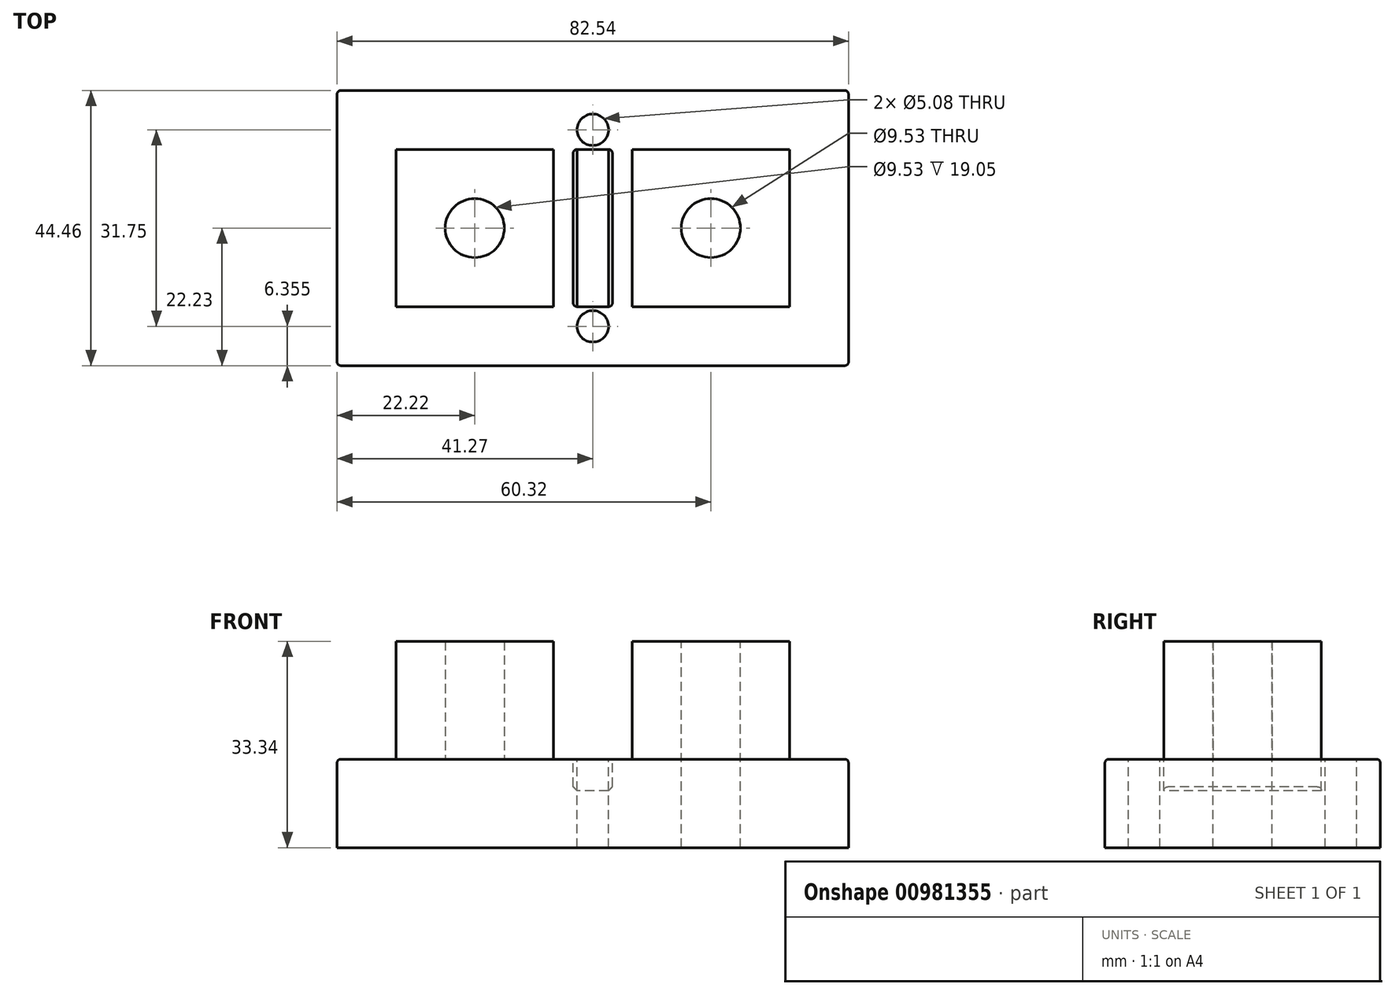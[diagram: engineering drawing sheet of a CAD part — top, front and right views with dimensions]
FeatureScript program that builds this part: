
annotation { "Feature Type Name" : "Feature", "Feature Type Description" : "" }
export const myFeature = defineFeature(function(context is Context, id is Id, definition is map)
    precondition{}
    {
        {
            var Q0;
            Q0=qCreatedBy(makeId("Top.planeOp"),FACE);
            var sketch = newSketch(context, id + "F0", { "sketchPlane" : qUnion([Q0])});
            skLineSegment(sketch, "E0.bottom", {"start": v(41.28, 22.23) * mm, "end": v(-41.28, 22.23) * mm});
            skLineSegment(sketch, "E0.top", {"start": v(41.28, -22.23) * mm, "end": v(-41.28, -22.23) * mm});
            skLineSegment(sketch, "E0.left", {"start": v(41.28, 22.23) * mm, "end": v(41.28, -22.23) * mm});
            skLineSegment(sketch, "E0.right", {"start": v(-41.28, 22.23) * mm, "end": v(-41.28, -22.23) * mm});
            skPoint(sketch, "E0.middle", {"position": v(0, 0) * mm});
            skLineSegment(sketch, "E1.bottom", {"start": v(31.75, 12.7) * mm, "end": v(6.35, 12.7) * mm});
            skLineSegment(sketch, "E1.top", {"start": v(31.75, -12.7) * mm, "end": v(6.35, -12.7) * mm});
            skLineSegment(sketch, "E1.left", {"start": v(31.75, 12.7) * mm, "end": v(31.75, -12.7) * mm});
            skLineSegment(sketch, "E1.right", {"start": v(-31.75, 12.7) * mm, "end": v(-31.75, -12.7) * mm});
            skLineSegment(sketch, "E2.bottom", {"start": v(6.35, 12.7) * mm, "end": v(-6.35, 12.7) * mm});
            skLineSegment(sketch, "E2.top", {"start": v(6.35, -12.7) * mm, "end": v(-6.35, -12.7) * mm});
            skLineSegment(sketch, "E2.left", {"start": v(6.35, 12.7) * mm, "end": v(6.35, -12.7) * mm});
            skLineSegment(sketch, "E2.right", {"start": v(-6.35, 12.7) * mm, "end": v(-6.35, 12.7) * mm});
            skLineSegment(sketch, "E3", {"start": v(-6.35, 12.7) * mm, "end": v(-6.35, -12.7) * mm});
            skLineSegment(sketch, "E4", {"start": v(-6.35, -12.7) * mm, "end": v(-31.75, -12.7) * mm});
            skLineSegment(sketch, "E5", {"start": v(-6.35, 12.7) * mm, "end": v(-31.75, 12.7) * mm});
            skCircle(sketch, "E6", {"center": v(-19.05, 0) * mm, "radius": 4.76 * mm});
            skCircle(sketch, "E7.MirrorC", {"center": v(19.05, 0) * mm, "radius": 4.76 * mm});
            skLineSegment(sketch, "E8.bottom", {"start": v(3.18, 22.23) * mm, "end": v(-3.18, 22.23) * mm});
            skLineSegment(sketch, "E8.top", {"start": v(3.18, -22.23) * mm, "end": v(-3.18, -22.23) * mm});
            skLineSegment(sketch, "E8.left", {"start": v(3.18, 22.23) * mm, "end": v(3.18, -22.23) * mm});
            skLineSegment(sketch, "E8.right", {"start": v(-3.18, 22.23) * mm, "end": v(-3.18, -22.23) * mm});
            skCircle(sketch, "E9", {"center": v(0, -15.88) * mm, "radius": 2.54 * mm});
            skLineSegment(sketch, "E10.bottom", {"start": v(-2.54, -22.23) * mm, "end": v(2.54, -22.23) * mm});
            skLineSegment(sketch, "E10.top", {"start": v(-2.54, 22.23) * mm, "end": v(2.54, 22.23) * mm});
            skCircle(sketch, "E11", {"center": v(0, 15.88) * mm, "radius": 2.54 * mm});
            skSolve(sketch);
        }
        {
            var Q0;
            {var subQ0=sQuery(id+"F0.wireOp",EDGE,"E0.right");Q0=makeQuery(id+"F0.imprint","IMPRINT",FACE,{"disambiguationData":[TD([[makeQuery(id+"F0.imprint","IMPRINT",EDGE,{"derivedFrom":subQ0}),1.0]])]});}
            var Q1;
            Q1=makeQuery(id+"F0.imprint","IMPRINT",FACE,{"disambiguationData":[TD([[makeQuery(id+"F0.imprint","IMPRINT",EDGE,{"derivedFrom":sQuery(id+"F0.wireOp",EDGE,"E1.right")}),1.0]])]});
            var Q2;
            {var subQ0=sQuery(id+"F0.wireOp",EDGE,"E3");Q2=makeQuery(id+"F0.imprint","IMPRINT",FACE,{"disambiguationData":[TD([[makeQuery(id+"F0.imprint","IMPRINT",EDGE,{"derivedFrom":subQ0}),1.0]])]});}
            var Q3;
            {var subQ0=sQuery(id+"F0.wireOp",EDGE,"E8.left");var subQ1=sQuery(id+"F0.wireOp",EDGE,"E2.top");var subQ2=makeQuery(id+"F0.imprint","INTERSECT",VERTEX,{"derivedFrom":[subQ1,subQ0]});Q3=makeQuery(id+"F0.imprint","IMPRINT",FACE,{"disambiguationData":[TD([[makeQuery(id+"F0.imprint","IMPRINT",EDGE,{"disambiguationData":[TD([[subQ2,-1.0]])],"derivedFrom":subQ1}),-1.0]])]});}
            var Q4;
            {var subQ5=sQuery(id+"F0.wireOp",EDGE,"E8.bottom");Q4=makeQuery(id+"F0.imprint","IMPRINT",FACE,{"disambiguationData":[TD([[makeQuery(id+"F0.imprint","IMPRINT",EDGE,{"derivedFrom":subQ5}),1.0]])]});}
            var Q5;
            {var subQ5=sQuery(id+"F0.wireOp",EDGE,"E8.top");Q5=makeQuery(id+"F0.imprint","IMPRINT",FACE,{"disambiguationData":[TD([[makeQuery(id+"F0.imprint","IMPRINT",EDGE,{"derivedFrom":subQ5}),-1.0]])]});}
            var Q6;
            {var subQ1=sQuery(id+"F0.wireOp",EDGE,"E0.left");Q6=makeQuery(id+"F0.imprint","IMPRINT",FACE,{"disambiguationData":[TD([[makeQuery(id+"F0.imprint","IMPRINT",EDGE,{"derivedFrom":subQ1}),-1.0]])]});}
            var Q7;
            {var subQ0=sQuery(id+"F0.wireOp",EDGE,"E2.left");Q7=makeQuery(id+"F0.imprint","IMPRINT",FACE,{"disambiguationData":[TD([[makeQuery(id+"F0.imprint","IMPRINT",EDGE,{"derivedFrom":subQ0}),-1.0]])]});}
            var Q8;
            Q8=makeQuery(id+"F0.imprint","IMPRINT",FACE,{"disambiguationData":[TD([[makeQuery(id+"F0.imprint","IMPRINT",EDGE,{"derivedFrom":sQuery(id+"F0.wireOp",EDGE,"E1.bottom")}),1.0]])]});
            var Q9;
            Q9=makeQuery(id+"F0.imprint","IMPRINT",FACE,{"disambiguationData":[TD([[makeQuery(id+"F0.imprint","IMPRINT",EDGE,{"derivedFrom":sQuery(id+"F0.wireOp",EDGE,"E7.MirrorC")}),-1.0]])]});
            var Q10;
            Q10=makeQuery(id+"F0.imprint","IMPRINT",FACE,{"disambiguationData":[TD([[makeQuery(id+"F0.imprint","IMPRINT",EDGE,{"derivedFrom":sQuery(id+"F0.wireOp",EDGE,"E6")}),1.0]])]});
            var Q11;
            {var subQ5=sQuery(id+"F0.wireOp",EDGE,"E10.bottom");Q11=makeQuery(id+"F0.imprint","IMPRINT",FACE,{"disambiguationData":[TD([[makeQuery(id+"F0.imprint","IMPRINT",EDGE,{"derivedFrom":subQ5}),1.0]])]});}
            var Q12;
            {var subQ0=sQuery(id+"F0.wireOp",EDGE,"E10.right");var subQ1=sQuery(id+"F0.wireOp",EDGE,"E2.top");var subQ2=makeQuery(id+"F0.imprint","INTERSECT",VERTEX,{"derivedFrom":[subQ1,subQ0]});Q12=makeQuery(id+"F0.imprint","IMPRINT",FACE,{"disambiguationData":[TD([[makeQuery(id+"F0.imprint","IMPRINT",EDGE,{"disambiguationData":[TD([[subQ2,-1.0]])],"derivedFrom":subQ1}),1.0]])]});}
            var Q13;
            {var subQ0=sQuery(id+"F0.wireOp",EDGE,"E10.right");var subQ1=sQuery(id+"F0.wireOp",EDGE,"E2.top");var subQ2=makeQuery(id+"F0.imprint","INTERSECT",VERTEX,{"derivedFrom":[subQ1,subQ0]});Q13=makeQuery(id+"F0.imprint","IMPRINT",FACE,{"disambiguationData":[TD([[makeQuery(id+"F0.imprint","IMPRINT",EDGE,{"disambiguationData":[TD([[subQ2,-1.0]])],"derivedFrom":subQ1}),-1.0]])]});}
            var Q14;
            {var subQ0=sQuery(id+"F0.wireOp",EDGE,"E9");var subQ1=makeQuery(id+"F0.imprint","INTERSECT",VERTEX,{"derivedFrom":[subQ0,sQuery(id+"F0.wireOp",EDGE,"E10.left")]});Q14=makeQuery(id+"F0.imprint","IMPRINT",FACE,{"disambiguationData":[TD([[makeQuery(id+"F0.imprint","IMPRINT",EDGE,{"disambiguationData":[TD([[subQ1,1.0]])],"derivedFrom":subQ0}),1.0]])]});}
            var Q15;
            {var subQ0=sQuery(id+"F0.wireOp",EDGE,"E11");var subQ1=makeQuery(id+"F0.imprint","INTERSECT",VERTEX,{"derivedFrom":[sQuery(id+"F0.wireOp",EDGE,"E10.left"),subQ0]});Q15=makeQuery(id+"F0.imprint","IMPRINT",FACE,{"disambiguationData":[TD([[makeQuery(id+"F0.imprint","IMPRINT",EDGE,{"disambiguationData":[TD([[subQ1,1.0]])],"derivedFrom":subQ0}),1.0]])]});}
            var Q16;
            {var subQ0=sQuery(id+"F0.wireOp",EDGE,"E10.top");Q16=makeQuery(id+"F0.imprint","IMPRINT",FACE,{"disambiguationData":[TD([[makeQuery(id+"F0.imprint","IMPRINT",EDGE,{"derivedFrom":subQ0}),-1.0]])]});}
            var Q17;
            {var subQ0=sQuery(id+"F0.wireOp",EDGE,"E10.left");var subQ1=sQuery(id+"F0.wireOp",EDGE,"E2.top");var subQ2=makeQuery(id+"F0.imprint","INTERSECT",VERTEX,{"derivedFrom":[subQ1,subQ0]});Q17=makeQuery(id+"F0.imprint","IMPRINT",FACE,{"disambiguationData":[TD([[makeQuery(id+"F0.imprint","IMPRINT",EDGE,{"disambiguationData":[TD([[subQ2,-1.0]])],"derivedFrom":subQ1}),-1.0]])]});}
            var Q18;
            {var subQ0=sQuery(id+"F0.wireOp",EDGE,"E10.right");var subQ1=sQuery(id+"F0.wireOp",EDGE,"E2.bottom");var subQ2=makeQuery(id+"F0.imprint","INTERSECT",VERTEX,{"derivedFrom":[subQ1,subQ0]});Q18=makeQuery(id+"F0.imprint","IMPRINT",FACE,{"disambiguationData":[TD([[makeQuery(id+"F0.imprint","IMPRINT",EDGE,{"disambiguationData":[TD([[subQ2,-1.0]])],"derivedFrom":subQ1}),-1.0]])]});}
            extrude(context, id + "F1", {"entities" : qUnion([Q0, Q1, Q2, Q3, Q4, Q5, Q6, Q7, Q8, Q9, Q10, Q11, Q12, Q13, Q14, Q15, Q16, Q17, Q18]), "oppositeDirection" : true, "depth" : 14.29 * mm, "offsetDistance" : 25.4 * mm});
        }
        {
            var Q0;
            Q0=makeQuery(id+"F0.imprint","IMPRINT",FACE,{"disambiguationData":[TD([[makeQuery(id+"F0.imprint","IMPRINT",EDGE,{"derivedFrom":sQuery(id+"F0.wireOp",EDGE,"E1.right")}),1.0]])]});
            var Q1;
            Q1=makeQuery(id+"F0.imprint","IMPRINT",FACE,{"disambiguationData":[TD([[makeQuery(id+"F0.imprint","IMPRINT",EDGE,{"derivedFrom":sQuery(id+"F0.wireOp",EDGE,"E1.bottom")}),1.0]])]});
            extrude(context, id + "F2", {"entities" : qUnion([Q0, Q1]), "operationType" : NewBodyOperationType.ADD, "depth" : 19.05 * mm, "offsetDistance" : 25.4 * mm});
        }
        {
            var Q0;
            {var subQ0=sQuery(id+"F0.wireOp",EDGE,"E8.left");var subQ1=sQuery(id+"F0.wireOp",EDGE,"E2.top");var subQ2=makeQuery(id+"F0.imprint","INTERSECT",VERTEX,{"derivedFrom":[subQ1,subQ0]});Q0=makeQuery(id+"F0.imprint","IMPRINT",FACE,{"disambiguationData":[TD([[makeQuery(id+"F0.imprint","IMPRINT",EDGE,{"disambiguationData":[TD([[subQ2,-1.0]])],"derivedFrom":subQ1}),-1.0]])]});}
            var Q1;
            {var subQ5=sQuery(id+"F0.wireOp",EDGE,"E8.top");Q1=makeQuery(id+"F0.imprint","IMPRINT",FACE,{"disambiguationData":[TD([[makeQuery(id+"F0.imprint","IMPRINT",EDGE,{"derivedFrom":subQ5}),-1.0]])]});}
            var Q2;
            {var subQ5=sQuery(id+"F0.wireOp",EDGE,"E8.bottom");Q2=makeQuery(id+"F0.imprint","IMPRINT",FACE,{"disambiguationData":[TD([[makeQuery(id+"F0.imprint","IMPRINT",EDGE,{"derivedFrom":subQ5}),1.0]])]});}
            extrude(context, id + "F3", {"entities" : qUnion([Q0, Q1, Q2]), "operationType" : NewBodyOperationType.REMOVE, "oppositeDirection" : true, "depth" : 5.08 * mm, "offsetDistance" : 25.4 * mm});
        }
        {
            var Q0;
            Q0=makeQuery(id+"F0.imprint","IMPRINT",FACE,{"disambiguationData":[TD([[makeQuery(id+"F0.imprint","IMPRINT",EDGE,{"derivedFrom":sQuery(id+"F0.wireOp",EDGE,"E9")}),1.0]])]});
            var Q1;
            Q1=makeQuery(id+"F0.imprint","IMPRINT",FACE,{"disambiguationData":[TD([[makeQuery(id+"F0.imprint","IMPRINT",EDGE,{"derivedFrom":sQuery(id+"F0.wireOp",EDGE,"E11")}),1.0]])]});
            extrude(context, id + "F4", {"entities" : qUnion([Q0, Q1]), "operationType" : NewBodyOperationType.REMOVE, "oppositeDirection" : true, "depth" : 14.29 * mm, "offsetDistance" : 25.4 * mm});
        }
        {
            var Q0;
            Q0=makeQuery(id+"F3.boolean.opBoolean","COPY",EDGE,{"derivedFrom":makeQuery(id+"F3.opExtrude","CAP_EDGE",EDGE,{"disambiguationData":[OSD([sQuery(id+"F0.wireOp",EDGE,"E8.left")])],"isStart":false})});
            var Q1;
            Q1=makeQuery(id+"F3.boolean.opBoolean","COPY",EDGE,{"derivedFrom":makeQuery(id+"F3.opExtrude","CAP_EDGE",EDGE,{"disambiguationData":[OSD([sQuery(id+"F0.wireOp",EDGE,"E8.right")])],"isStart":false})});
            var Q2;
            Q2=makeQuery(id+"F3.boolean.opBoolean","COPY",EDGE,{"derivedFrom":makeQuery(id+"F3.opExtrude","CAP_EDGE",EDGE,{"disambiguationData":[OSD([sQuery(id+"F0.wireOp",EDGE,"E8.left")])],"isStart":true})});
            var Q3;
            Q3=makeQuery(id+"F3.boolean.opBoolean","COPY",EDGE,{"derivedFrom":makeQuery(id+"F3.opExtrude","CAP_EDGE",EDGE,{"disambiguationData":[OSD([sQuery(id+"F0.wireOp",EDGE,"E8.right")])],"isStart":true})});
            chamfer(context, id + "F5", {"entities" : qUnion([Q0, Q1, Q2, Q3]), "width" : 0.64 * mm, "tangentPropagation" : true});
        }
        {
            var Q0;
            {var subQ0=sQuery(id+"F0.wireOp",EDGE,"E10.bottom");var subQ1=sQuery(id+"F0.wireOp",EDGE,"E8.top");var subQ2=sQuery(id+"F0.wireOp",EDGE,"E0.right");var subQ3=sQuery(id+"F0.wireOp",EDGE,"E0.top");Q0=makeQuery(id+"F3.boolean.opBoolean","SPLIT",EDGE,{"disambiguationData":[TD([makeQuery(id+"F1.opExtrude","SWEPT_FACE",FACE,{"disambiguationData":[OSD([subQ2])]})])],"derivedFrom":makeQuery(id+"F1.opExtrude","CAP_EDGE",EDGE,{"disambiguationData":[OSD([subQ3,subQ1,subQ0])],"isStart":true})});}
            var Q1;
            Q1=makeQuery(id+"F5.opChamfer","BLEND_EDGE",EDGE,{"blendedFrom":[makeQuery(id+"F3.boolean.opBoolean","COPY",EDGE,{"derivedFrom":makeQuery(id+"F3.opExtrude","CAP_EDGE",EDGE,{"disambiguationData":[OSD([sQuery(id+"F0.wireOp",EDGE,"E8.right")])],"isStart":true})}),makeQuery(id+"F1.opExtrude","SWEPT_FACE",FACE,{"disambiguationData":[OSD([sQuery(id+"F0.wireOp",EDGE,"E0.top"),sQuery(id+"F0.wireOp",EDGE,"E8.top"),sQuery(id+"F0.wireOp",EDGE,"E10.bottom")])]})],"blendedInto":[makeQuery(id+"F1.opExtrude","SWEPT_FACE",FACE,{"disambiguationData":[OSD([sQuery(id+"F0.wireOp",EDGE,"E0.top"),sQuery(id+"F0.wireOp",EDGE,"E8.top"),sQuery(id+"F0.wireOp",EDGE,"E10.bottom")])]})]});
            var Q2;
            Q2=makeQuery(id+"F5.opChamfer","BLEND_EDGE",EDGE,{"blendedFrom":[makeQuery(id+"F3.boolean.opBoolean","COPY",EDGE,{"derivedFrom":makeQuery(id+"F3.opExtrude","CAP_EDGE",EDGE,{"disambiguationData":[OSD([sQuery(id+"F0.wireOp",EDGE,"E8.right")])],"isStart":false})}),makeQuery(id+"F1.opExtrude","SWEPT_FACE",FACE,{"disambiguationData":[OSD([sQuery(id+"F0.wireOp",EDGE,"E0.top"),sQuery(id+"F0.wireOp",EDGE,"E8.top"),sQuery(id+"F0.wireOp",EDGE,"E10.bottom")])]})],"blendedInto":[makeQuery(id+"F1.opExtrude","SWEPT_FACE",FACE,{"disambiguationData":[OSD([sQuery(id+"F0.wireOp",EDGE,"E0.top"),sQuery(id+"F0.wireOp",EDGE,"E8.top"),sQuery(id+"F0.wireOp",EDGE,"E10.bottom")])]})]});
            var Q3;
            Q3=makeQuery(id+"F3.boolean.opBoolean","COPY",EDGE,{"derivedFrom":makeQuery(id+"F3.opExtrude","CAP_EDGE",EDGE,{"disambiguationData":[OSD([sQuery(id+"F0.wireOp",EDGE,"E8.top"),sQuery(id+"F0.wireOp",EDGE,"E10.bottom")])],"isStart":false})});
            var Q4;
            Q4=makeQuery(id+"F5.opChamfer","BLEND_EDGE",EDGE,{"blendedFrom":[makeQuery(id+"F3.boolean.opBoolean","COPY",EDGE,{"derivedFrom":makeQuery(id+"F3.opExtrude","CAP_EDGE",EDGE,{"disambiguationData":[OSD([sQuery(id+"F0.wireOp",EDGE,"E8.left")])],"isStart":false})}),makeQuery(id+"F1.opExtrude","SWEPT_FACE",FACE,{"disambiguationData":[OSD([sQuery(id+"F0.wireOp",EDGE,"E0.top"),sQuery(id+"F0.wireOp",EDGE,"E8.top"),sQuery(id+"F0.wireOp",EDGE,"E10.bottom")])]})],"blendedInto":[makeQuery(id+"F1.opExtrude","SWEPT_FACE",FACE,{"disambiguationData":[OSD([sQuery(id+"F0.wireOp",EDGE,"E0.top"),sQuery(id+"F0.wireOp",EDGE,"E8.top"),sQuery(id+"F0.wireOp",EDGE,"E10.bottom")])]})]});
            var Q5;
            Q5=makeQuery(id+"F3.boolean.opBoolean","COPY",EDGE,{"derivedFrom":makeQuery(id+"F3.opExtrude","SWEPT_EDGE",EDGE,{"disambiguationData":[OSD([sQuery(id+"F0.wireOp",EDGE,"E0.top"),sQuery(id+"F0.wireOp",EDGE,"E8.top"),sQuery(id+"F0.wireOp",EDGE,"E8.left")])]})});
            var Q6;
            Q6=makeQuery(id+"F5.opChamfer","BLEND_EDGE",EDGE,{"blendedFrom":[makeQuery(id+"F3.boolean.opBoolean","COPY",EDGE,{"derivedFrom":makeQuery(id+"F3.opExtrude","CAP_EDGE",EDGE,{"disambiguationData":[OSD([sQuery(id+"F0.wireOp",EDGE,"E8.left")])],"isStart":true})}),makeQuery(id+"F1.opExtrude","SWEPT_FACE",FACE,{"disambiguationData":[OSD([sQuery(id+"F0.wireOp",EDGE,"E0.top"),sQuery(id+"F0.wireOp",EDGE,"E8.top"),sQuery(id+"F0.wireOp",EDGE,"E10.bottom")])]})],"blendedInto":[makeQuery(id+"F1.opExtrude","SWEPT_FACE",FACE,{"disambiguationData":[OSD([sQuery(id+"F0.wireOp",EDGE,"E0.top"),sQuery(id+"F0.wireOp",EDGE,"E8.top"),sQuery(id+"F0.wireOp",EDGE,"E10.bottom")])]})]});
            var Q7;
            {var subQ0=sQuery(id+"F0.wireOp",EDGE,"E10.bottom");var subQ1=sQuery(id+"F0.wireOp",EDGE,"E8.top");var subQ2=sQuery(id+"F0.wireOp",EDGE,"E0.left");var subQ3=sQuery(id+"F0.wireOp",EDGE,"E0.top");Q7=makeQuery(id+"F3.boolean.opBoolean","SPLIT",EDGE,{"disambiguationData":[TD([makeQuery(id+"F1.opExtrude","SWEPT_FACE",FACE,{"disambiguationData":[OSD([subQ2])]})])],"derivedFrom":makeQuery(id+"F1.opExtrude","CAP_EDGE",EDGE,{"disambiguationData":[OSD([subQ3,subQ1,subQ0])],"isStart":true})});}
            var Q8;
            Q8=makeQuery(id+"F1.opExtrude","SWEPT_EDGE",EDGE,{"disambiguationData":[OSD([sQuery(id+"F0.wireOp",EDGE,"E0.top"),sQuery(id+"F0.wireOp",EDGE,"E0.right")])]});
            var Q9;
            Q9=makeQuery(id+"F1.opExtrude","CAP_EDGE",EDGE,{"disambiguationData":[OSD([sQuery(id+"F0.wireOp",EDGE,"E0.right")])],"isStart":true});
            var Q10;
            Q10=makeQuery(id+"F1.opExtrude","SWEPT_EDGE",EDGE,{"disambiguationData":[OSD([sQuery(id+"F0.wireOp",EDGE,"E0.bottom"),sQuery(id+"F0.wireOp",EDGE,"E0.right")])]});
            var Q11;
            {var subQ0=sQuery(id+"F0.wireOp",EDGE,"E10.top");var subQ1=sQuery(id+"F0.wireOp",EDGE,"E8.bottom");var subQ2=sQuery(id+"F0.wireOp",EDGE,"E0.right");var subQ3=sQuery(id+"F0.wireOp",EDGE,"E0.bottom");Q11=makeQuery(id+"F3.boolean.opBoolean","SPLIT",EDGE,{"disambiguationData":[TD([makeQuery(id+"F1.opExtrude","SWEPT_FACE",FACE,{"disambiguationData":[OSD([subQ2])]})])],"derivedFrom":makeQuery(id+"F1.opExtrude","CAP_EDGE",EDGE,{"disambiguationData":[OSD([subQ3,subQ1,subQ0])],"isStart":true})});}
            var Q12;
            Q12=makeQuery(id+"F3.boolean.opBoolean","COPY",EDGE,{"derivedFrom":makeQuery(id+"F3.opExtrude","SWEPT_EDGE",EDGE,{"disambiguationData":[OSD([sQuery(id+"F0.wireOp",EDGE,"E0.bottom"),sQuery(id+"F0.wireOp",EDGE,"E8.bottom"),sQuery(id+"F0.wireOp",EDGE,"E8.right")])]})});
            var Q13;
            Q13=makeQuery(id+"F5.opChamfer","BLEND_EDGE",EDGE,{"blendedFrom":[makeQuery(id+"F3.boolean.opBoolean","COPY",EDGE,{"derivedFrom":makeQuery(id+"F3.opExtrude","CAP_EDGE",EDGE,{"disambiguationData":[OSD([sQuery(id+"F0.wireOp",EDGE,"E8.right")])],"isStart":true})}),makeQuery(id+"F1.opExtrude","SWEPT_FACE",FACE,{"disambiguationData":[OSD([sQuery(id+"F0.wireOp",EDGE,"E0.bottom"),sQuery(id+"F0.wireOp",EDGE,"E8.bottom"),sQuery(id+"F0.wireOp",EDGE,"E10.top")])]})],"blendedInto":[makeQuery(id+"F1.opExtrude","SWEPT_FACE",FACE,{"disambiguationData":[OSD([sQuery(id+"F0.wireOp",EDGE,"E0.bottom"),sQuery(id+"F0.wireOp",EDGE,"E8.bottom"),sQuery(id+"F0.wireOp",EDGE,"E10.top")])]})]});
            var Q14;
            Q14=makeQuery(id+"F3.boolean.opBoolean","COPY",EDGE,{"derivedFrom":makeQuery(id+"F3.opExtrude","CAP_EDGE",EDGE,{"disambiguationData":[OSD([sQuery(id+"F0.wireOp",EDGE,"E8.bottom"),sQuery(id+"F0.wireOp",EDGE,"E10.top")])],"isStart":false})});
            var Q15;
            Q15=makeQuery(id+"F5.opChamfer","BLEND_EDGE",EDGE,{"blendedFrom":[makeQuery(id+"F3.boolean.opBoolean","COPY",EDGE,{"derivedFrom":makeQuery(id+"F3.opExtrude","CAP_EDGE",EDGE,{"disambiguationData":[OSD([sQuery(id+"F0.wireOp",EDGE,"E8.right")])],"isStart":false})}),makeQuery(id+"F1.opExtrude","SWEPT_FACE",FACE,{"disambiguationData":[OSD([sQuery(id+"F0.wireOp",EDGE,"E0.bottom"),sQuery(id+"F0.wireOp",EDGE,"E8.bottom"),sQuery(id+"F0.wireOp",EDGE,"E10.top")])]})],"blendedInto":[makeQuery(id+"F1.opExtrude","SWEPT_FACE",FACE,{"disambiguationData":[OSD([sQuery(id+"F0.wireOp",EDGE,"E0.bottom"),sQuery(id+"F0.wireOp",EDGE,"E8.bottom"),sQuery(id+"F0.wireOp",EDGE,"E10.top")])]})]});
            var Q16;
            {var subQ0=sQuery(id+"F0.wireOp",EDGE,"E10.top");var subQ1=sQuery(id+"F0.wireOp",EDGE,"E8.bottom");var subQ2=sQuery(id+"F0.wireOp",EDGE,"E0.left");var subQ3=sQuery(id+"F0.wireOp",EDGE,"E0.bottom");Q16=makeQuery(id+"F3.boolean.opBoolean","SPLIT",EDGE,{"disambiguationData":[TD([makeQuery(id+"F1.opExtrude","SWEPT_FACE",FACE,{"disambiguationData":[OSD([subQ2])]})])],"derivedFrom":makeQuery(id+"F1.opExtrude","CAP_EDGE",EDGE,{"disambiguationData":[OSD([subQ3,subQ1,subQ0])],"isStart":true})});}
            var Q17;
            Q17=makeQuery(id+"F3.boolean.opBoolean","COPY",EDGE,{"derivedFrom":makeQuery(id+"F3.opExtrude","SWEPT_EDGE",EDGE,{"disambiguationData":[OSD([sQuery(id+"F0.wireOp",EDGE,"E0.bottom"),sQuery(id+"F0.wireOp",EDGE,"E8.bottom"),sQuery(id+"F0.wireOp",EDGE,"E8.left")])]})});
            var Q18;
            Q18=makeQuery(id+"F5.opChamfer","BLEND_EDGE",EDGE,{"blendedFrom":[makeQuery(id+"F3.boolean.opBoolean","COPY",EDGE,{"derivedFrom":makeQuery(id+"F3.opExtrude","CAP_EDGE",EDGE,{"disambiguationData":[OSD([sQuery(id+"F0.wireOp",EDGE,"E8.left")])],"isStart":true})}),makeQuery(id+"F1.opExtrude","SWEPT_FACE",FACE,{"disambiguationData":[OSD([sQuery(id+"F0.wireOp",EDGE,"E0.bottom"),sQuery(id+"F0.wireOp",EDGE,"E8.bottom"),sQuery(id+"F0.wireOp",EDGE,"E10.top")])]})],"blendedInto":[makeQuery(id+"F1.opExtrude","SWEPT_FACE",FACE,{"disambiguationData":[OSD([sQuery(id+"F0.wireOp",EDGE,"E0.bottom"),sQuery(id+"F0.wireOp",EDGE,"E8.bottom"),sQuery(id+"F0.wireOp",EDGE,"E10.top")])]})]});
            var Q19;
            Q19=makeQuery(id+"F1.opExtrude","SWEPT_EDGE",EDGE,{"disambiguationData":[OSD([sQuery(id+"F0.wireOp",EDGE,"E0.bottom"),sQuery(id+"F0.wireOp",EDGE,"E0.left")])]});
            var Q20;
            Q20=makeQuery(id+"F1.opExtrude","CAP_EDGE",EDGE,{"disambiguationData":[OSD([sQuery(id+"F0.wireOp",EDGE,"E0.left")])],"isStart":true});
            var Q21;
            Q21=makeQuery(id+"F1.opExtrude","SWEPT_EDGE",EDGE,{"disambiguationData":[OSD([sQuery(id+"F0.wireOp",EDGE,"E0.top"),sQuery(id+"F0.wireOp",EDGE,"E0.left")])]});
            var Q22;
            Q22=makeQuery(id+"F5.opChamfer","BLEND_EDGE",EDGE,{"blendedFrom":[makeQuery(id+"F3.boolean.opBoolean","COPY",EDGE,{"derivedFrom":makeQuery(id+"F3.opExtrude","CAP_EDGE",EDGE,{"disambiguationData":[OSD([sQuery(id+"F0.wireOp",EDGE,"E8.left")])],"isStart":false})}),makeQuery(id+"F1.opExtrude","SWEPT_FACE",FACE,{"disambiguationData":[OSD([sQuery(id+"F0.wireOp",EDGE,"E0.bottom"),sQuery(id+"F0.wireOp",EDGE,"E8.bottom"),sQuery(id+"F0.wireOp",EDGE,"E10.top")])]})],"blendedInto":[makeQuery(id+"F1.opExtrude","SWEPT_FACE",FACE,{"disambiguationData":[OSD([sQuery(id+"F0.wireOp",EDGE,"E0.bottom"),sQuery(id+"F0.wireOp",EDGE,"E8.bottom"),sQuery(id+"F0.wireOp",EDGE,"E10.top")])]})]});
            var Q23;
            Q23=makeQuery(id+"F3.boolean.opBoolean","COPY",EDGE,{"derivedFrom":makeQuery(id+"F3.opExtrude","SWEPT_EDGE",EDGE,{"disambiguationData":[OSD([sQuery(id+"F0.wireOp",EDGE,"E0.top"),sQuery(id+"F0.wireOp",EDGE,"E8.top"),sQuery(id+"F0.wireOp",EDGE,"E8.right")])]})});
            fillet(context, id + "F6", {"entities" : qUnion([Q0, Q1, Q2, Q3, Q4, Q5, Q6, Q7, Q8, Q9, Q10, Q11, Q12, Q13, Q14, Q15, Q16, Q17, Q18, Q19, Q20, Q21, Q22, Q23]), "radius" : 0.64 * mm, "tangentPropagation" : true, "allowEdgeOverflow" : false});
        }
    });
